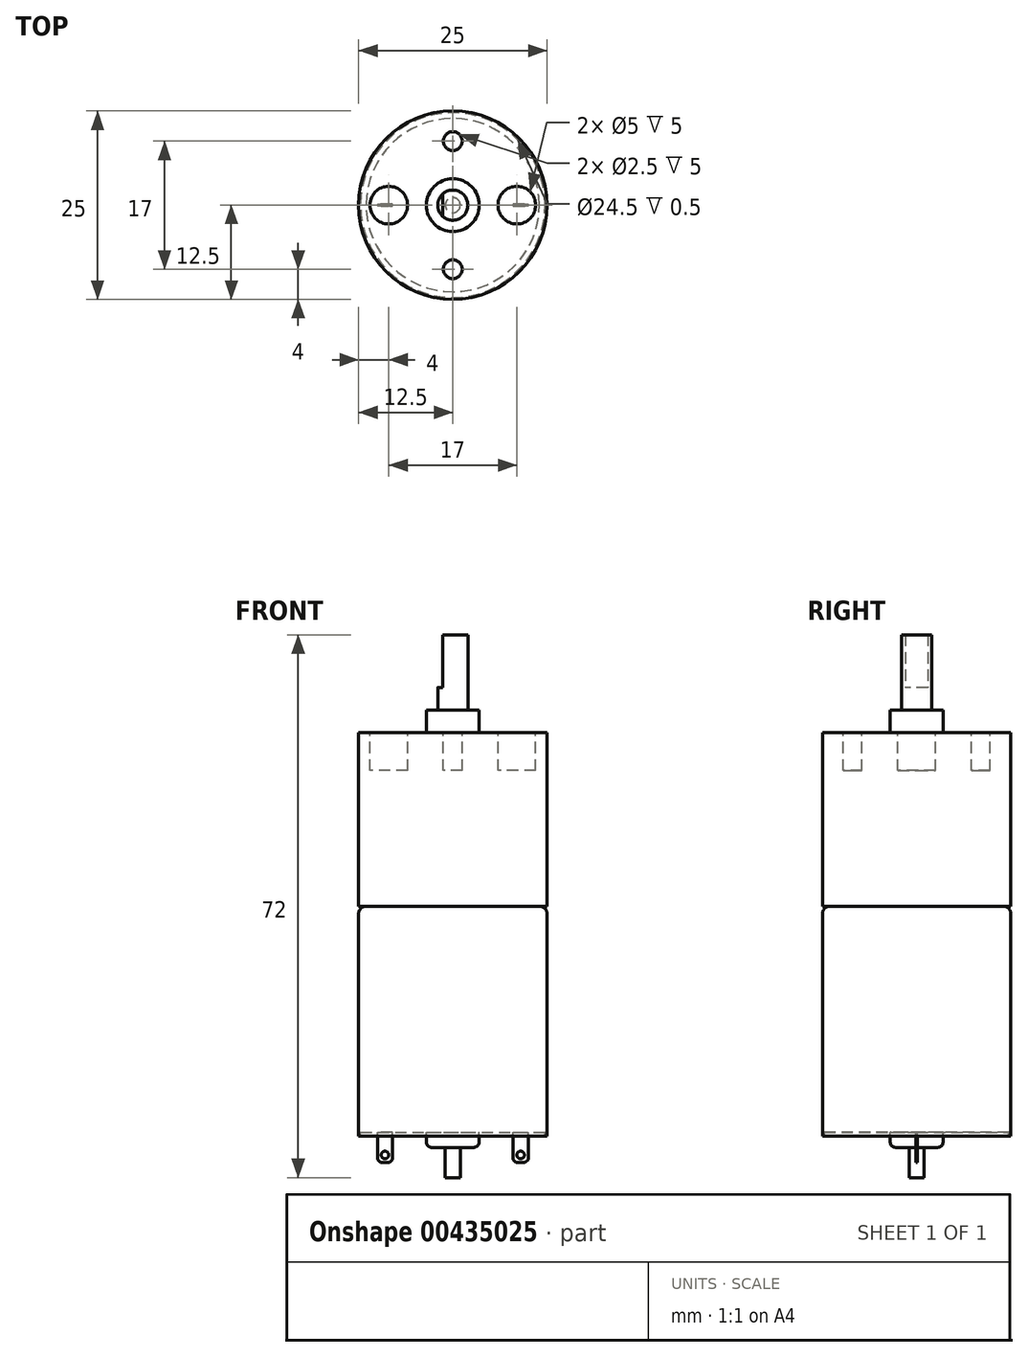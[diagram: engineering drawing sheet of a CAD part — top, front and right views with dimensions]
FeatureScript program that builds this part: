
annotation { "Feature Type Name" : "Feature", "Feature Type Description" : "" }
export const myFeature = defineFeature(function(context is Context, id is Id, definition is map)
    precondition{}
    {
        {
            var Q0;
            Q0=qCreatedBy(makeId("Top.planeOp"),FACE);
            var sketch = newSketch(context, id + "F0", { "sketchPlane" : qUnion([Q0])});
            skCircle(sketch, "E0", {"center": v(0, 0) * mm, "radius": 12.5 * mm});
            skSolve(sketch);
        }
        {
            var Q0;
            Q0=makeQuery(id+"F0.imprint","IMPRINT",FACE,{"disambiguationData":[TD([[makeQuery(id+"F0.imprint","IMPRINT",EDGE,{"derivedFrom":sQuery(id+"F0.wireOp",EDGE,"E0")}),1.0]])]});
            extrude(context, id + "F1", {"entities" : qUnion([Q0]), "depth" : 30 * mm});
        }
        {
            var Q0;
            Q0=makeQuery(id+"F1.opExtrude","CAP_EDGE",EDGE,{"disambiguationData":[OSD([sQuery(id+"F0.wireOp",EDGE,"E0")])],"isStart":false});
            fillet(context, id + "F2", {"entities" : qUnion([Q0]), "radius" : 1 * mm, "tangentPropagation" : true, "allowEdgeOverflow" : false});
        }
        {
            var Q0;
            Q0=makeQuery(id+"F1.opExtrude","CAP_FACE",FACE,{"disambiguationData":[OSD([sQuery(id+"F0.wireOp",EDGE,"E0")])],"isStart":false});
            var sketch = newSketch(context, id + "F3", { "sketchPlane" : qUnion([Q0])});
            skCircle(sketch, "E1.0", {"center": v(0, 0) * mm, "radius": 12.5 * mm});
            skSolve(sketch);
        }
        {
            var Q0;
            Q0 = qSketchRegion(id + "F3", true);
            extrude(context, id + "F4", {"entities" : qUnion([Q0]), "operationType" : NewBodyOperationType.ADD, "depth" : 23 * mm});
        }
        {
            var Q0;
            Q0=makeQuery(id+"F4.opExtrude","CAP_FACE",FACE,{"disambiguationData":[OSD([sQuery(id+"F3.wireOp",EDGE,"E1.0")])],"isStart":false});
            var sketch = newSketch(context, id + "F5", { "sketchPlane" : qUnion([Q0])});
            skCircle(sketch, "E2", {"center": v(0, 0) * mm, "radius": 3.5 * mm});
            skSolve(sketch);
        }
        {
            var Q0;
            Q0 = qSketchRegion(id + "F5", true);
            extrude(context, id + "F6", {"entities" : qUnion([Q0]), "operationType" : NewBodyOperationType.ADD, "depth" : 3 * mm});
        }
        {
            var Q0;
            Q0=makeQuery(id+"F6.opExtrude","CAP_FACE",FACE,{"disambiguationData":[OSD([sQuery(id+"F5.wireOp",EDGE,"E2")])],"isStart":false});
            var sketch = newSketch(context, id + "F7", { "sketchPlane" : qUnion([Q0])});
            skCircle(sketch, "E3", {"center": v(0, 0) * mm, "radius": 2 * mm});
            skSolve(sketch);
        }
        {
            var Q0;
            Q0=makeQuery(id+"F7.imprint","IMPRINT",FACE,{"disambiguationData":[TD([[makeQuery(id+"F7.imprint","IMPRINT",EDGE,{"derivedFrom":sQuery(id+"F7.wireOp",EDGE,"E3")}),1.0]])]});
            var Q1;
            Q1 = qConstructionFilter(qBodyType(qCreatedBy(id + "F7" ,EDGE), BodyType.WIRE), ConstructionObject.NO);
            extrude(context, id + "F8", {"entities" : qUnion([Q0]), "surfaceEntities" : qUnion([Q1]), "depth" : 3 * mm});
        }
        {
            var Q0;
            Q0=makeQuery(id+"F8.opExtrude","CAP_FACE",FACE,{"disambiguationData":[OSD([sQuery(id+"F7.wireOp",EDGE,"E3")])],"isStart":false});
            var sketch = newSketch(context, id + "F9", { "sketchPlane" : qUnion([Q0])});
            skArc(sketch, "E4", {"start": v(-1.32, 1.5) * mm, "mid": v(2, 0) * mm, "end": v(-1.32, -1.5) * mm});
            skLineSegment(sketch, "E5", {"start": v(-1.32, 1.5) * mm, "end": v(-1.32, -1.5) * mm});
            skSolve(sketch);
        }
        {
            var Q0;
            Q0=makeQuery(id+"F9.imprint","IMPRINT",FACE,{"disambiguationData":[TD([[makeQuery(id+"F9.imprint","IMPRINT",EDGE,{"derivedFrom":sQuery(id+"F9.wireOp",EDGE,"E4")}),1.0]])]});
            extrude(context, id + "F10", {"entities" : qUnion([Q0]), "operationType" : NewBodyOperationType.ADD, "depth" : 7 * mm});
        }
        {
            var Q0;
            Q0=makeQuery(id+"F1.opExtrude","CAP_FACE",FACE,{"disambiguationData":[OSD([sQuery(id+"F0.wireOp",EDGE,"E0")])],"isStart":true});
            var sketch = newSketch(context, id + "F11", { "sketchPlane" : qUnion([Q0])});
            skCircle(sketch, "E6", {"center": v(0, 0) * mm, "radius": 3.5 * mm});
            skSolve(sketch);
        }
        {
            var Q0;
            Q0=makeQuery(id+"F11.imprint","IMPRINT",FACE,{"disambiguationData":[TD([[makeQuery(id+"F11.imprint","IMPRINT",EDGE,{"derivedFrom":sQuery(id+"F11.wireOp",EDGE,"E6")}),1.0]])]});
            extrude(context, id + "F12", {"entities" : qUnion([Q0]), "operationType" : NewBodyOperationType.ADD, "depth" : 2 * mm});
        }
        {
            var Q0;
            Q0=makeQuery(id+"F12.opExtrude","CAP_EDGE",EDGE,{"disambiguationData":[OSD([sQuery(id+"F11.wireOp",EDGE,"E6")])],"isStart":false});
            fillet(context, id + "F13", {"entities" : qUnion([Q0]), "radius" : .7 * mm, "tangentPropagation" : true, "allowEdgeOverflow" : false});
        }
        {
            var Q0;
            Q0=makeQuery(id+"F12.opExtrude","CAP_FACE",FACE,{"disambiguationData":[OSD([sQuery(id+"F11.wireOp",EDGE,"E6")])],"isStart":false});
            var sketch = newSketch(context, id + "F14", { "sketchPlane" : qUnion([Q0])});
            skCircle(sketch, "E7", {"center": v(0, 0) * mm, "radius": 1 * mm});
            skSolve(sketch);
        }
        {
            var Q0;
            Q0 = qSketchRegion(id + "F14", true);
            extrude(context, id + "F15", {"entities" : qUnion([Q0]), "operationType" : NewBodyOperationType.ADD, "depth" : 4 * mm});
        }
        {
            var Q0;
            Q0=makeQuery(id+"F1.opExtrude","CAP_FACE",FACE,{"disambiguationData":[OSD([sQuery(id+"F0.wireOp",EDGE,"E0")])],"isStart":true});
            var sketch = newSketch(context, id + "F16", { "sketchPlane" : qUnion([Q0])});
            skCircle(sketch, "E8.0", {"center": v(0, 0) * mm, "radius": 12.5 * mm});
            skCircle(sketch, "E9", {"center": v(0, 0) * mm, "radius": 12.25 * mm});
            skSolve(sketch);
        }
        {
            var Q0;
            Q0 = qSketchRegion(id + "F16", true);
            extrude(context, id + "F17", {"entities" : qUnion([Q0]), "operationType" : NewBodyOperationType.ADD, "depth" : .5 * mm});
        }
        {
            var Q0;
            Q0=makeQuery(id+"F1.opExtrude","CAP_FACE",FACE,{"disambiguationData":[OSD([sQuery(id+"F0.wireOp",EDGE,"E0")])],"isStart":true});
            var sketch = newSketch(context, id + "F18", { "sketchPlane" : qUnion([Q0])});
            skLineSegment(sketch, "E10.bottom", {"start": v(-8, -0.12) * mm, "end": v(-10, -0.12) * mm});
            skLineSegment(sketch, "E10.top", {"start": v(-8, 0.13) * mm, "end": v(-10, 0.13) * mm});
            skLineSegment(sketch, "E10.left", {"start": v(-8, -0.12) * mm, "end": v(-8, 0.13) * mm});
            skLineSegment(sketch, "E10.right", {"start": v(-10, -0.12) * mm, "end": v(-10, 0.13) * mm});
            skPoint(sketch, "E10.middle", {"position": v(-9, 0) * mm});
            skSolve(sketch);
        }
        {
            var Q0;
            Q0=makeQuery(id+"F18.imprint","IMPRINT",FACE,{"disambiguationData":[TD([[makeQuery(id+"F18.imprint","IMPRINT",EDGE,{"derivedFrom":sQuery(id+"F18.wireOp",EDGE,"E10.bottom")}),-1.0]])]});
            extrude(context, id + "F19", {"entities" : qUnion([Q0]), "depth" : 4 * mm});
        }
        {
            var Q0;
            Q0=makeQuery(id+"F19.opExtrude","CAP_EDGE",EDGE,{"disambiguationData":[OSD([sQuery(id+"F18.wireOp",EDGE,"E10.right")])],"isStart":false});
            var Q1;
            Q1=makeQuery(id+"F19.opExtrude","CAP_EDGE",EDGE,{"disambiguationData":[OSD([sQuery(id+"F18.wireOp",EDGE,"E10.left")])],"isStart":false});
            chamfer(context, id + "F20", {"entities" : qUnion([Q0, Q1]), "width" : .4 * mm, "tangentPropagation" : true});
        }
        {
            var Q0;
            Q0=makeQuery(id+"F19.opExtrude","SWEPT_FACE",FACE,{"disambiguationData":[OSD([sQuery(id+"F18.wireOp",EDGE,"E10.top")])]});
            var sketch = newSketch(context, id + "F21", { "sketchPlane" : qUnion([Q0])});
            skCircle(sketch, "E11", {"center": v(-9, -3) * mm, "radius": 0.5 * mm});
            skLineSegment(sketch, "E12", {"start": v(-10, -3) * mm, "end": v(-8, -3) * mm, "construction": true});
            skSolve(sketch);
        }
        {
            var Q0;
            Q0=makeQuery(id+"F21.imprint","IMPRINT",FACE,{"disambiguationData":[TD([[makeQuery(id+"F21.imprint","IMPRINT",EDGE,{"derivedFrom":sQuery(id+"F21.wireOp",EDGE,"E11")}),1.0]])]});
            extrude(context, id + "F22", {"entities" : qUnion([Q0]), "operationType" : NewBodyOperationType.REMOVE, "oppositeDirection" : true, "depth" : 25 * mm});
        }
        {
            var Q0;
            Q0=makeQuery(id+"F19.opExtrude","SWEPT_BODY",BODY,{"disambiguationData":[OSD([sQuery(id+"F18.wireOp",EDGE,"E10.bottom"),sQuery(id+"F18.wireOp",EDGE,"E10.top"),sQuery(id+"F18.wireOp",EDGE,"E10.left"),sQuery(id+"F18.wireOp",EDGE,"E10.right")])]});
            var Q1;
            Q1=makeQuery(id+"F15.opExtrude","SWEPT_FACE",FACE,{"disambiguationData":[OSD([sQuery(id+"F14.wireOp",EDGE,"E7")])]});
            circularPattern(context, id + "F23", {"entities" : qUnion([Q0]), "axis" : qUnion([Q1]), "angle" : 180 * degree, "instanceCount" : 2, "equalSpace" : true});
        }
        {
            var Q0;
            Q0=makeQuery(id+"F4.opExtrude","CAP_FACE",FACE,{"disambiguationData":[OSD([sQuery(id+"F3.wireOp",EDGE,"E1.0")])],"isStart":false});
            var sketch = newSketch(context, id + "F24", { "sketchPlane" : qUnion([Q0])});
            skCircle(sketch, "E13", {"center": v(-8.5, 0) * mm, "radius": 2.5 * mm});
            skCircle(sketch, "E14", {"center": v(8.5, 0) * mm, "radius": 2.5 * mm});
            skCircle(sketch, "E15", {"center": v(0, 8.5) * mm, "radius": 1.25 * mm});
            skCircle(sketch, "E16", {"center": v(0, -8.5) * mm, "radius": 1.25 * mm});
            skCircle(sketch, "E17", {"center": v(0, 0) * mm, "radius": 8.5 * mm, "construction": true});
            skSolve(sketch);
        }
        {
            var Q0;
            Q0=makeQuery(id+"F24.imprint","IMPRINT",FACE,{"disambiguationData":[TD([[makeQuery(id+"F24.imprint","IMPRINT",EDGE,{"derivedFrom":sQuery(id+"F24.wireOp",EDGE,"E15")}),1.0]])]});
            var Q1;
            Q1=makeQuery(id+"F24.imprint","IMPRINT",FACE,{"disambiguationData":[TD([[makeQuery(id+"F24.imprint","IMPRINT",EDGE,{"derivedFrom":sQuery(id+"F24.wireOp",EDGE,"E13")}),1.0]])]});
            var Q2;
            Q2=makeQuery(id+"F24.imprint","IMPRINT",FACE,{"disambiguationData":[TD([[makeQuery(id+"F24.imprint","IMPRINT",EDGE,{"derivedFrom":sQuery(id+"F24.wireOp",EDGE,"E16")}),1.0]])]});
            var Q3;
            Q3=makeQuery(id+"F24.imprint","IMPRINT",FACE,{"disambiguationData":[TD([[makeQuery(id+"F24.imprint","IMPRINT",EDGE,{"derivedFrom":sQuery(id+"F24.wireOp",EDGE,"E14")}),1.0]])]});
            extrude(context, id + "F25", {"entities" : qUnion([Q0, Q1, Q2, Q3]), "operationType" : NewBodyOperationType.REMOVE, "oppositeDirection" : true, "depth" : 5 * mm});
        }
    });
